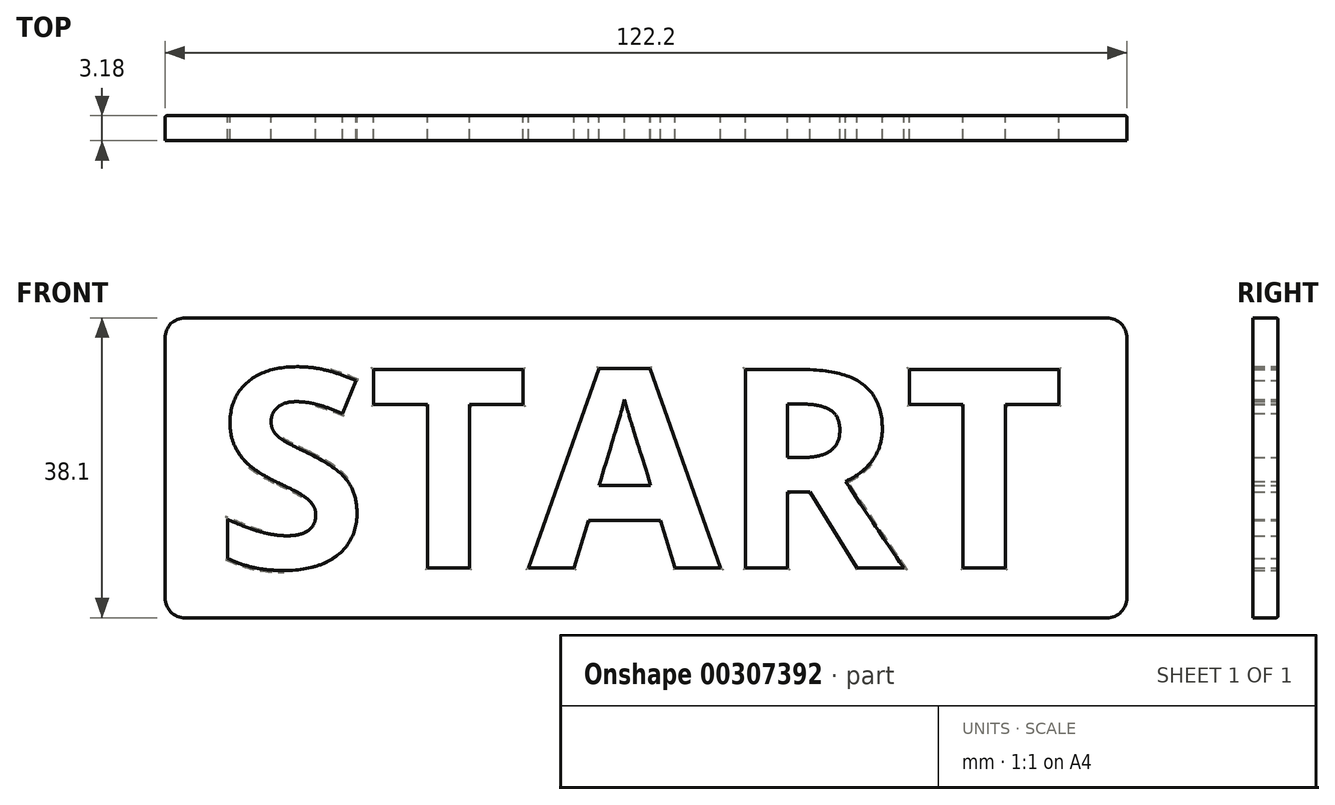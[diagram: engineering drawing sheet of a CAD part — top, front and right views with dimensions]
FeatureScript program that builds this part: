
annotation { "Feature Type Name" : "Feature", "Feature Type Description" : "" }
export const myFeature = defineFeature(function(context is Context, id is Id, definition is map)
    precondition{}
    {
        {
            var Q0;
            Q0=qCreatedBy(makeId("Front.planeOp"),FACE);
            var sketch = newSketch(context, id + "F0", { "sketchPlane" : qUnion([Q0])});
            skText(sketch, "E0", { "text": "START", "fontName": "OpenSans-Bold.ttf"});
            skLineSegment(sketch, "E1.bottom", {"start": v(-6.35, -6.35) * mm, "end": v(115.85, -6.35) * mm});
            skLineSegment(sketch, "E1.top", {"start": v(-6.35, 31.75) * mm, "end": v(115.85, 31.75) * mm});
            skLineSegment(sketch, "E1.left", {"start": v(-6.35, -6.35) * mm, "end": v(-6.35, 31.75) * mm});
            skLineSegment(sketch, "E1.right", {"start": v(115.85, -6.35) * mm, "end": v(115.85, 31.75) * mm});
            const initialGuessF0  = {"E0": [0, 0, 1, 0, 0.0254]};
            skSetInitialGuess(sketch, initialGuessF0);
            skSolve(sketch);
        }
        {
            var Q0;
            Q0 = qSketchRegion(id + "F0", true);
            var Q1;
            Q1=makeQuery(id+"F0.imprint","IMPRINT",FACE,{"disambiguationData":[TD([[makeQuery(id+"F0.imprint","IMPRINT",EDGE,{"derivedFrom":sQuery(id+"F0.wireOp",EDGE,"E0.sketch_text.stroke-48")}),1.0]])]});
            var Q2;
            Q2=makeQuery(id+"F0.imprint","IMPRINT",FACE,{"disambiguationData":[TD([[makeQuery(id+"F0.imprint","IMPRINT",EDGE,{"derivedFrom":sQuery(id+"F0.wireOp",EDGE,"E0.sketch_text.stroke-44")}),1.0]])]});
            extrude(context, id + "F1", {"entities" : qUnion([Q0, Q1, Q2]), "depth" : 3.17 * mm});
        }
        {
            var Q0;
            Q0=makeQuery(id+"F1.opExtrude","SWEPT_EDGE",EDGE,{"disambiguationData":[OSD([sQuery(id+"F0.wireOp",EDGE,"E1.bottom"),sQuery(id+"F0.wireOp",EDGE,"E1.left")])]});
            var Q1;
            Q1=makeQuery(id+"F1.opExtrude","SWEPT_EDGE",EDGE,{"disambiguationData":[OSD([sQuery(id+"F0.wireOp",EDGE,"E1.top"),sQuery(id+"F0.wireOp",EDGE,"E1.left")])]});
            var Q2;
            Q2=makeQuery(id+"F1.opExtrude","SWEPT_EDGE",EDGE,{"disambiguationData":[OSD([sQuery(id+"F0.wireOp",EDGE,"E1.bottom"),sQuery(id+"F0.wireOp",EDGE,"E1.right")])]});
            var Q3;
            Q3=makeQuery(id+"F1.opExtrude","SWEPT_EDGE",EDGE,{"disambiguationData":[OSD([sQuery(id+"F0.wireOp",EDGE,"E1.top"),sQuery(id+"F0.wireOp",EDGE,"E1.right")])]});
            fillet(context, id + "F2", {"entities" : qUnion([Q0, Q1, Q2, Q3]), "radius" : 2.54 * mm, "tangentPropagation" : true, "allowEdgeOverflow" : false});
        }
        {
            var Q0;
            Q0=makeQuery(id+"F1.opExtrude","CAP_FACE",FACE,{"disambiguationData":[OSD([sQuery(id+"F0.wireOp",EDGE,"E0.sketch_text.stroke-0"),sQuery(id+"F0.wireOp",EDGE,"E0.sketch_text.stroke-1"),sQuery(id+"F0.wireOp",EDGE,"E0.sketch_text.stroke-2"),sQuery(id+"F0.wireOp",EDGE,"E0.sketch_text.stroke-3"),sQuery(id+"F0.wireOp",EDGE,"E0.sketch_text.stroke-4"),sQuery(id+"F0.wireOp",EDGE,"E0.sketch_text.stroke-5"),sQuery(id+"F0.wireOp",EDGE,"E0.sketch_text.stroke-6"),sQuery(id+"F0.wireOp",EDGE,"E0.sketch_text.stroke-7"),sQuery(id+"F0.wireOp",EDGE,"E0.sketch_text.stroke-8"),sQuery(id+"F0.wireOp",EDGE,"E0.sketch_text.stroke-9"),sQuery(id+"F0.wireOp",EDGE,"E0.sketch_text.stroke-10"),sQuery(id+"F0.wireOp",EDGE,"E0.sketch_text.stroke-11"),sQuery(id+"F0.wireOp",EDGE,"E0.sketch_text.stroke-12"),sQuery(id+"F0.wireOp",EDGE,"E0.sketch_text.stroke-13"),sQuery(id+"F0.wireOp",EDGE,"E0.sketch_text.stroke-14"),sQuery(id+"F0.wireOp",EDGE,"E0.sketch_text.stroke-15"),sQuery(id+"F0.wireOp",EDGE,"E0.sketch_text.stroke-16"),sQuery(id+"F0.wireOp",EDGE,"E0.sketch_text.stroke-17"),sQuery(id+"F0.wireOp",EDGE,"E0.sketch_text.stroke-18"),sQuery(id+"F0.wireOp",EDGE,"E0.sketch_text.stroke-19"),sQuery(id+"F0.wireOp",EDGE,"E0.sketch_text.stroke-20"),sQuery(id+"F0.wireOp",EDGE,"E0.sketch_text.stroke-21"),sQuery(id+"F0.wireOp",EDGE,"E0.sketch_text.stroke-22"),sQuery(id+"F0.wireOp",EDGE,"E0.sketch_text.stroke-23"),sQuery(id+"F0.wireOp",EDGE,"E0.sketch_text.stroke-24"),sQuery(id+"F0.wireOp",EDGE,"E0.sketch_text.stroke-25"),sQuery(id+"F0.wireOp",EDGE,"E0.sketch_text.stroke-26"),sQuery(id+"F0.wireOp",EDGE,"E0.sketch_text.stroke-27"),sQuery(id+"F0.wireOp",EDGE,"E0.sketch_text.stroke-28"),sQuery(id+"F0.wireOp",EDGE,"E0.sketch_text.stroke-29"),sQuery(id+"F0.wireOp",EDGE,"E0.sketch_text.stroke-30"),sQuery(id+"F0.wireOp",EDGE,"E0.sketch_text.stroke-31"),sQuery(id+"F0.wireOp",EDGE,"E0.sketch_text.stroke-32"),sQuery(id+"F0.wireOp",EDGE,"E0.sketch_text.stroke-33"),sQuery(id+"F0.wireOp",EDGE,"E0.sketch_text.stroke-34"),sQuery(id+"F0.wireOp",EDGE,"E0.sketch_text.stroke-35"),sQuery(id+"F0.wireOp",EDGE,"E0.sketch_text.stroke-36"),sQuery(id+"F0.wireOp",EDGE,"E0.sketch_text.stroke-37"),sQuery(id+"F0.wireOp",EDGE,"E0.sketch_text.stroke-38"),sQuery(id+"F0.wireOp",EDGE,"E0.sketch_text.stroke-39"),sQuery(id+"F0.wireOp",EDGE,"E0.sketch_text.stroke-40"),sQuery(id+"F0.wireOp",EDGE,"E0.sketch_text.stroke-41"),sQuery(id+"F0.wireOp",EDGE,"E0.sketch_text.stroke-42"),sQuery(id+"F0.wireOp",EDGE,"E0.sketch_text.stroke-43"),sQuery(id+"F0.wireOp",EDGE,"E0.sketch_text.stroke-55"),sQuery(id+"F0.wireOp",EDGE,"E0.sketch_text.stroke-56"),sQuery(id+"F0.wireOp",EDGE,"E0.sketch_text.stroke-57"),sQuery(id+"F0.wireOp",EDGE,"E0.sketch_text.stroke-58"),sQuery(id+"F0.wireOp",EDGE,"E0.sketch_text.stroke-59"),sQuery(id+"F0.wireOp",EDGE,"E0.sketch_text.stroke-60"),sQuery(id+"F0.wireOp",EDGE,"E0.sketch_text.stroke-61"),sQuery(id+"F0.wireOp",EDGE,"E0.sketch_text.stroke-62"),sQuery(id+"F0.wireOp",EDGE,"E0.sketch_text.stroke-63"),sQuery(id+"F0.wireOp",EDGE,"E0.sketch_text.stroke-64"),sQuery(id+"F0.wireOp",EDGE,"E0.sketch_text.stroke-65"),sQuery(id+"F0.wireOp",EDGE,"E0.sketch_text.stroke-66"),sQuery(id+"F0.wireOp",EDGE,"E0.sketch_text.stroke-67"),sQuery(id+"F0.wireOp",EDGE,"E0.sketch_text.stroke-68"),sQuery(id+"F0.wireOp",EDGE,"E0.sketch_text.stroke-69"),sQuery(id+"F0.wireOp",EDGE,"E0.sketch_text.stroke-70"),sQuery(id+"F0.wireOp",EDGE,"E0.sketch_text.stroke-71"),sQuery(id+"F0.wireOp",EDGE,"E0.sketch_text.stroke-72"),sQuery(id+"F0.wireOp",EDGE,"E0.sketch_text.stroke-73"),sQuery(id+"F0.wireOp",EDGE,"E0.sketch_text.stroke-74"),sQuery(id+"F0.wireOp",EDGE,"E1.bottom"),sQuery(id+"F0.wireOp",EDGE,"E1.top"),sQuery(id+"F0.wireOp",EDGE,"E1.left"),sQuery(id+"F0.wireOp",EDGE,"E1.right")])],"isStart":true});
            fillet(context, id + "F3", {"entities" : qUnion([Q0]), "radius" : 0.25 * mm, "tangentPropagation" : true, "allowEdgeOverflow" : false});
        }
    });
